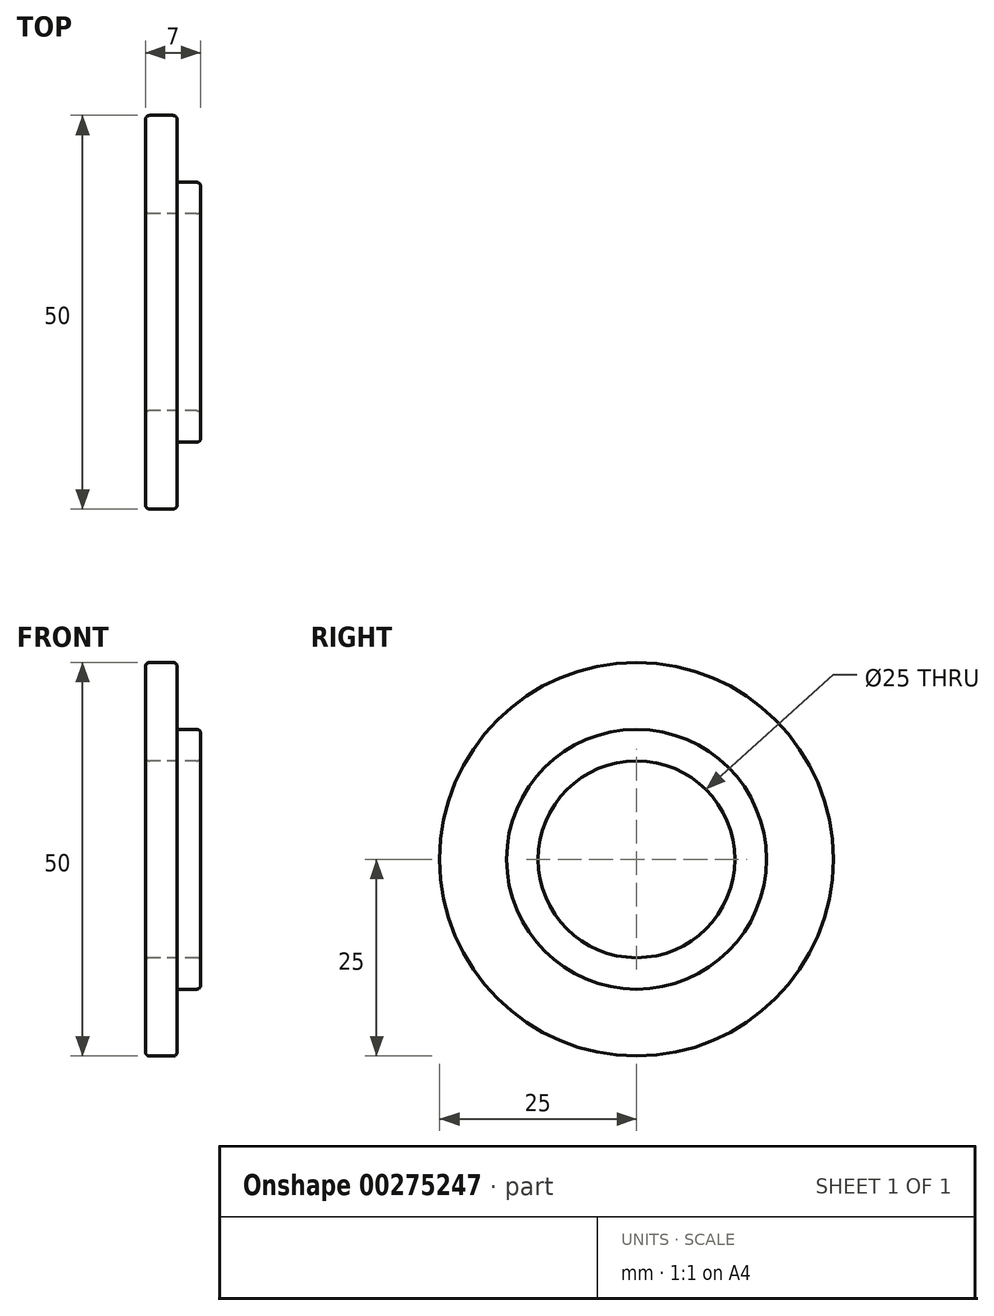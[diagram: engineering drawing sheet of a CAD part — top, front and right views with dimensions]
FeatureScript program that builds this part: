
annotation { "Feature Type Name" : "Feature", "Feature Type Description" : "" }
export const myFeature = defineFeature(function(context is Context, id is Id, definition is map)
    precondition{}
    {
        {
            var Q0;
            Q0=qCreatedBy(makeId("Front.planeOp"),FACE);
            var sketch = newSketch(context, id + "F0", { "sketchPlane" : qUnion([Q0])});
            skLineSegment(sketch, "E0", {"start": v(0, 0) * mm, "end": v(0, 12.5) * mm});
            skLineSegment(sketch, "E1", {"start": v(0, 12.5) * mm, "end": v(4, 12.5) * mm});
            skLineSegment(sketch, "E2", {"start": v(4, 12.5) * mm, "end": v(4, 4) * mm});
            skLineSegment(sketch, "E3", {"start": v(4, 4) * mm, "end": v(7, 4) * mm});
            skLineSegment(sketch, "E4", {"start": v(7, 4) * mm, "end": v(7, 0) * mm});
            skLineSegment(sketch, "E5", {"start": v(7, 0) * mm, "end": v(0, 0) * mm});
            skLineSegment(sketch, "E6", {"start": v(-16.82, -12.5) * mm, "end": v(24.53, -12.5) * mm, "construction": true});
            skSolve(sketch);
        }
        {
            var Q0;
            Q0 = qSketchRegion(id + "F0", true);
            var Q1;
            Q1=sQuery(id+"F0.wireOp",EDGE,"E6");
            revolve(context, id + "F1", {"entities" : qUnion([Q0]), "axis" : qUnion([Q1]), "revolveType" : RevolveType.FULL});
        }
        {
            var Q0;
            Q0=makeQuery(id+"F1.opRevolve","SWEPT_EDGE",EDGE,{"disambiguationData":[OSD([sQuery(id+"F0.wireOp",EDGE,"E3"),sQuery(id+"F0.wireOp",EDGE,"E4")])]});
            var Q1;
            Q1=makeQuery(id+"F1.opRevolve","SWEPT_EDGE",EDGE,{"disambiguationData":[OSD([sQuery(id+"F0.wireOp",EDGE,"E4"),sQuery(id+"F0.wireOp",EDGE,"E5")])]});
            var Q2;
            Q2=makeQuery(id+"F1.opRevolve","SWEPT_EDGE",EDGE,{"disambiguationData":[OSD([sQuery(id+"F0.wireOp",EDGE,"E1"),sQuery(id+"F0.wireOp",EDGE,"E2")])]});
            var Q3;
            Q3=makeQuery(id+"F1.opRevolve","SWEPT_EDGE",EDGE,{"disambiguationData":[OSD([sQuery(id+"F0.wireOp",EDGE,"E0"),sQuery(id+"F0.wireOp",EDGE,"E5")])]});
            var Q4;
            Q4=makeQuery(id+"F1.opRevolve","SWEPT_EDGE",EDGE,{"disambiguationData":[OSD([sQuery(id+"F0.wireOp",EDGE,"E0"),sQuery(id+"F0.wireOp",EDGE,"E1")])]});
            fillet(context, id + "F2", {"entities" : qUnion([Q0, Q1, Q2, Q3, Q4]), "radius" : .5 * mm, "tangentPropagation" : true, "allowEdgeOverflow" : false});
        }
    });
